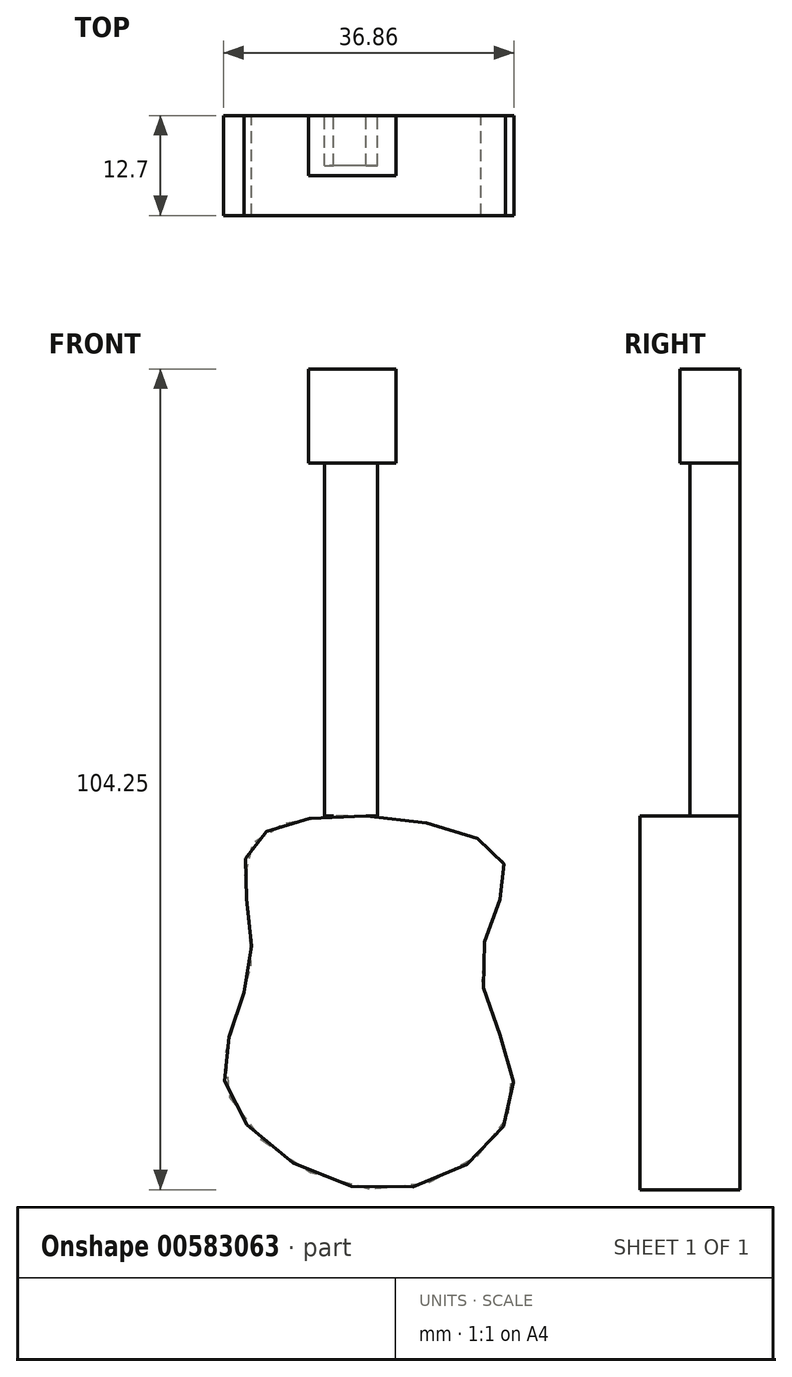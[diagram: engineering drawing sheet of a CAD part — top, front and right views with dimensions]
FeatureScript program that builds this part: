
annotation { "Feature Type Name" : "Feature", "Feature Type Description" : "" }
export const myFeature = defineFeature(function(context is Context, id is Id, definition is map)
    precondition{}
    {
        {
            var Q0;
            Q0=qCreatedBy(makeId("Front.planeOp"),FACE);
            var sketch = newSketch(context, id + "F0", { "sketchPlane" : qUnion([Q0])});
            skFitSpline(sketch, "E0", {"points": [v(-51.54, -18.54) * mm, v(-54.75, -34.31) * mm, v(-34.9, -47.45) * mm, v(-18.25, -36.06) * mm, v(-22.34, -18.83) * mm, v(-19.42, -5.99) * mm, v(-36.94, 0) * mm, v(-51.83, -4.23) * mm, v(-51.54, -18.54) * mm]});
            skLineSegment(sketch, "E1.bottom", {"start": v(-36.94, 0) * mm, "end": v(-36.94, 0) * mm});
            skLineSegment(sketch, "E1.top", {"start": v(-36.94, 43.95) * mm, "end": v(-36.94, 43.95) * mm});
            skLineSegment(sketch, "E1.left", {"start": v(-36.94, 0) * mm, "end": v(-36.94, 43.95) * mm});
            skLineSegment(sketch, "E1.right", {"start": v(-36.94, 0) * mm, "end": v(-36.94, 43.95) * mm});
            skLineSegment(sketch, "E2.bottom", {"start": v(-36.94, 35.48) * mm, "end": v(-29.35, 35.48) * mm});
            skLineSegment(sketch, "E2.top", {"start": v(-36.94, 35.19) * mm, "end": v(-29.35, 35.19) * mm});
            skLineSegment(sketch, "E2.left", {"start": v(-36.94, 35.48) * mm, "end": v(-36.94, 35.19) * mm});
            skLineSegment(sketch, "E2.right", {"start": v(-29.35, 35.48) * mm, "end": v(-29.35, 35.19) * mm});
            skSolve(sketch);
        }
        {
            var Q0;
            Q0=makeQuery(id+"F0.imprint","IMPRINT",FACE,{"disambiguationData":[TD([[makeQuery(id+"F0.imprint","IMPRINT",EDGE,{"derivedFrom":sQuery(id+"F0.wireOp",EDGE,"E0")}),1.0]])]});
            extrude(context, id + "F1", {"entities" : qUnion([Q0]), "depth" : 12.7 * mm, "offsetDistance" : 25.4 * mm});
        }
        {
            var Q0;
            Q0=qCreatedBy(makeId("Front.planeOp"),FACE);
            var sketch = newSketch(context, id + "F2", { "sketchPlane" : qUnion([Q0])});
            skLineSegment(sketch, "E3.bottom", {"start": v(-42.2, 0) * mm, "end": v(-35.48, 0) * mm});
            skLineSegment(sketch, "E3.top", {"start": v(-42.2, 48.04) * mm, "end": v(-35.48, 48.04) * mm});
            skLineSegment(sketch, "E3.left", {"start": v(-42.2, 0) * mm, "end": v(-42.2, 48.04) * mm});
            skLineSegment(sketch, "E3.right", {"start": v(-35.48, 0) * mm, "end": v(-35.48, 48.04) * mm});
            skSolve(sketch);
        }
        {
            var Q0;
            Q0=makeQuery(id+"F2.imprint","IMPRINT",FACE,{"disambiguationData":[TD([[makeQuery(id+"F2.imprint","IMPRINT",EDGE,{"derivedFrom":sQuery(id+"F2.wireOp",EDGE,"E3.bottom")}),1.0]])]});
            extrude(context, id + "F3", {"entities" : qUnion([Q0]), "operationType" : NewBodyOperationType.ADD, "depth" : 6.35 * mm, "offsetDistance" : 25.4 * mm});
        }
        {
            var Q0;
            Q0=qCreatedBy(makeId("Front.planeOp"),FACE);
            var sketch = newSketch(context, id + "F4", { "sketchPlane" : qUnion([Q0])});
            skCircle(sketch, "E4", {"center": v(-36.94, -12.41) * mm, "radius": 7.02 * mm});
            skSolve(sketch);
        }
        {
            var Q0;
            Q0 = qSketchRegion(id + "F4", true);
            extrude(context, id + "F5", {"entities" : qUnion([Q0]), "operationType" : NewBodyOperationType.ADD, "depth" : 1.78 * mm, "offsetDistance" : 25.4 * mm});
        }
        {
            var Q0;
            Q0=qCreatedBy(makeId("Front.planeOp"),FACE);
            var sketch = newSketch(context, id + "F6", { "sketchPlane" : qUnion([Q0])});
            skLineSegment(sketch, "E5.bottom", {"start": v(-44.24, 56.8) * mm, "end": v(-33.14, 56.8) * mm});
            skLineSegment(sketch, "E5.top", {"start": v(-44.24, 44.82) * mm, "end": v(-33.14, 44.82) * mm});
            skLineSegment(sketch, "E5.left", {"start": v(-44.24, 56.8) * mm, "end": v(-44.24, 44.82) * mm});
            skLineSegment(sketch, "E5.right", {"start": v(-33.14, 56.8) * mm, "end": v(-33.14, 44.82) * mm});
            skSolve(sketch);
        }
        {
            var Q0;
            Q0 = qSketchRegion(id + "F6", true);
            extrude(context, id + "F7", {"entities" : qUnion([Q0]), "operationType" : NewBodyOperationType.ADD, "depth" : 7.62 * mm, "offsetDistance" : 25.4 * mm});
        }
        {
            var Q0;
            Q0=qCreatedBy(makeId("Front.planeOp"),FACE);
            var sketch = newSketch(context, id + "F8", { "sketchPlane" : qUnion([Q0])});
            skCircle(sketch, "E6", {"center": v(-38.98, -11.83) * mm, "radius": 9 * mm});
            skSolve(sketch);
        }
        {
            var Q0;
            Q0 = qSketchRegion(id + "F8", true);
            extrude(context, id + "F9", {"entities" : qUnion([Q0]), "operationType" : NewBodyOperationType.ADD, "depth" : 0.76 * mm, "offsetDistance" : 25.4 * mm});
        }
    });
